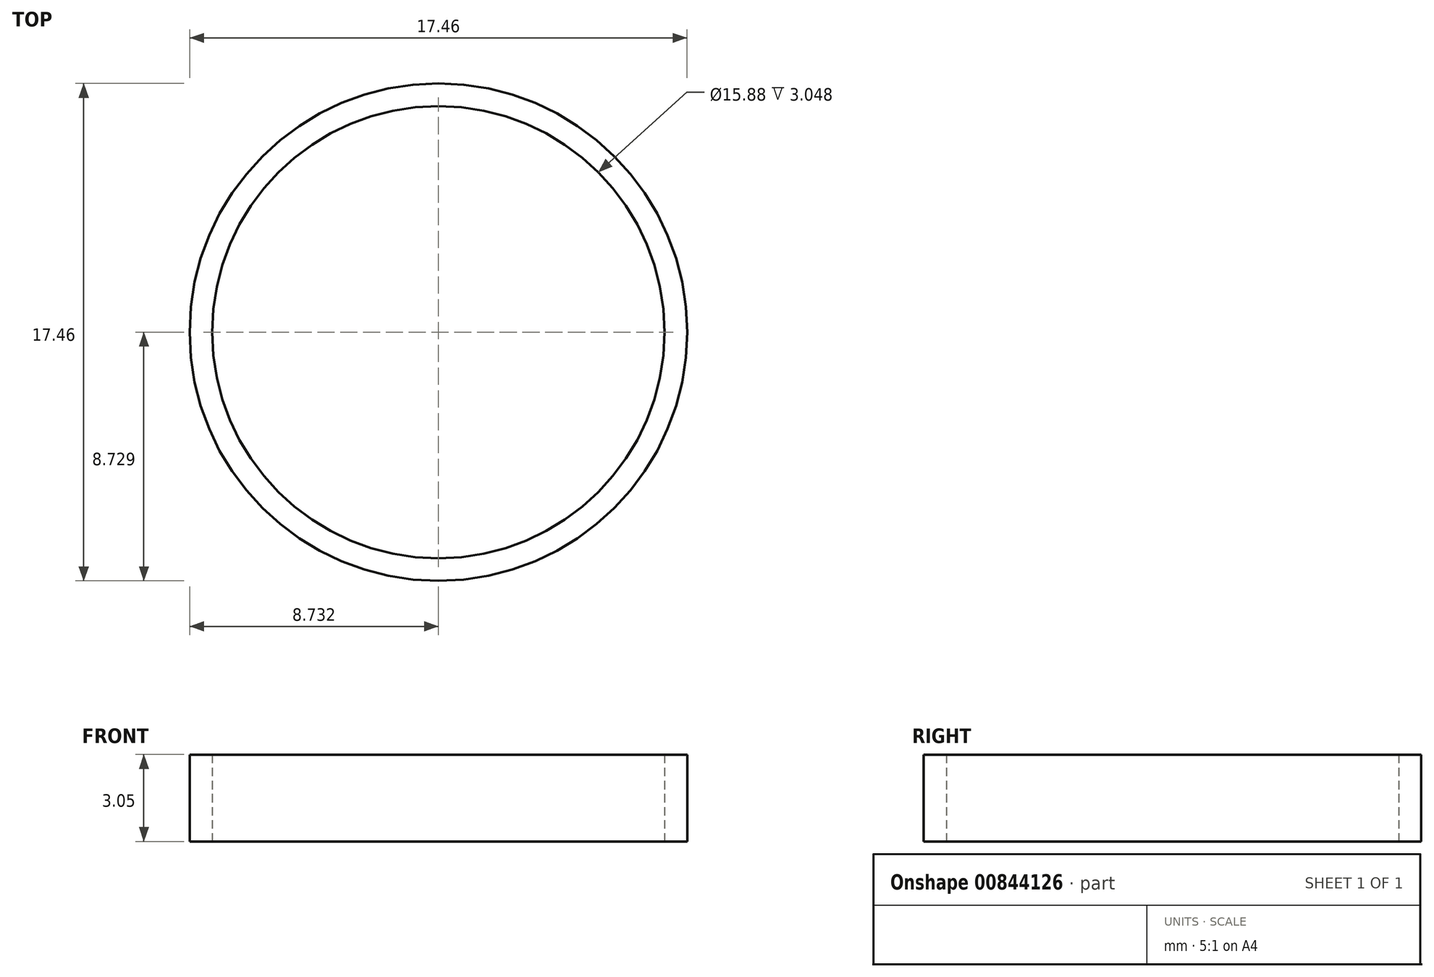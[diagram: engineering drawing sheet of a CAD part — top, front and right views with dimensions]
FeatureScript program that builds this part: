
annotation { "Feature Type Name" : "Feature", "Feature Type Description" : "" }
export const myFeature = defineFeature(function(context is Context, id is Id, definition is map)
    precondition{}
    {
        {
            var Q0;
            Q0=qCreatedBy(makeId("Top.planeOp"),FACE);
            var sketch = newSketch(context, id + "F0", { "sketchPlane" : qUnion([Q0])});
            skCircle(sketch, "E0", {"center": v(-49.5, 35.1) * mm, "radius": 7.94 * mm});
            skCircle(sketch, "E1", {"center": v(-49.5, 35.1) * mm, "radius": 8.73 * mm});
            skSolve(sketch);
        }
        {
            var Q0;
            Q0=makeQuery(id+"F0.imprint","IMPRINT",FACE,{"disambiguationData":[TD([[makeQuery(id+"F0.imprint","IMPRINT",EDGE,{"derivedFrom":sQuery(id+"F0.wireOp",EDGE,"E0")}),-1.0]])]});
            extrude(context, id + "F1", {"entities" : qUnion([Q0]), "depth" : 3.05 * mm, "offsetDistance" : 25.4 * mm});
        }
    });
